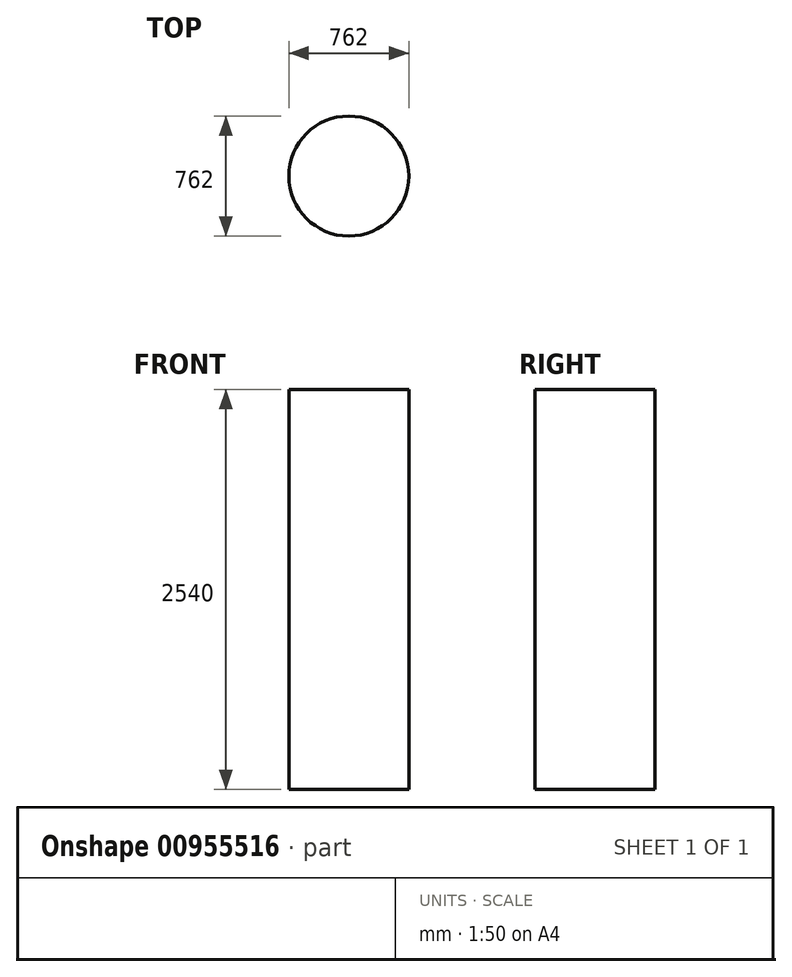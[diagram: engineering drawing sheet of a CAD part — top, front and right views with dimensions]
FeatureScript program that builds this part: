
annotation { "Feature Type Name" : "Feature", "Feature Type Description" : "" }
export const myFeature = defineFeature(function(context is Context, id is Id, definition is map)
    precondition{}
    {
        {
            var Q0;
            Q0=qCreatedBy(makeId("Top.planeOp"),FACE);
            var sketch = newSketch(context, id + "F0", { "sketchPlane" : qUnion([Q0])});
            skCircle(sketch, "E0", {"center": v(0, 0) * mm, "radius": 381 * mm});
            skSolve(sketch);
        }
        {
            var Q0;
            Q0=makeQuery(id+"F0.imprint","IMPRINT",FACE,{"disambiguationData":[TD([[makeQuery(id+"F0.imprint","IMPRINT",EDGE,{"derivedFrom":sQuery(id+"F0.wireOp",EDGE,"E0")}),1.0]])]});
            extrude(context, id + "F1", {"entities" : qUnion([Q0]), "depth" : 2540 * mm, "offsetDistance" : 25.4 * mm});
        }
    });
